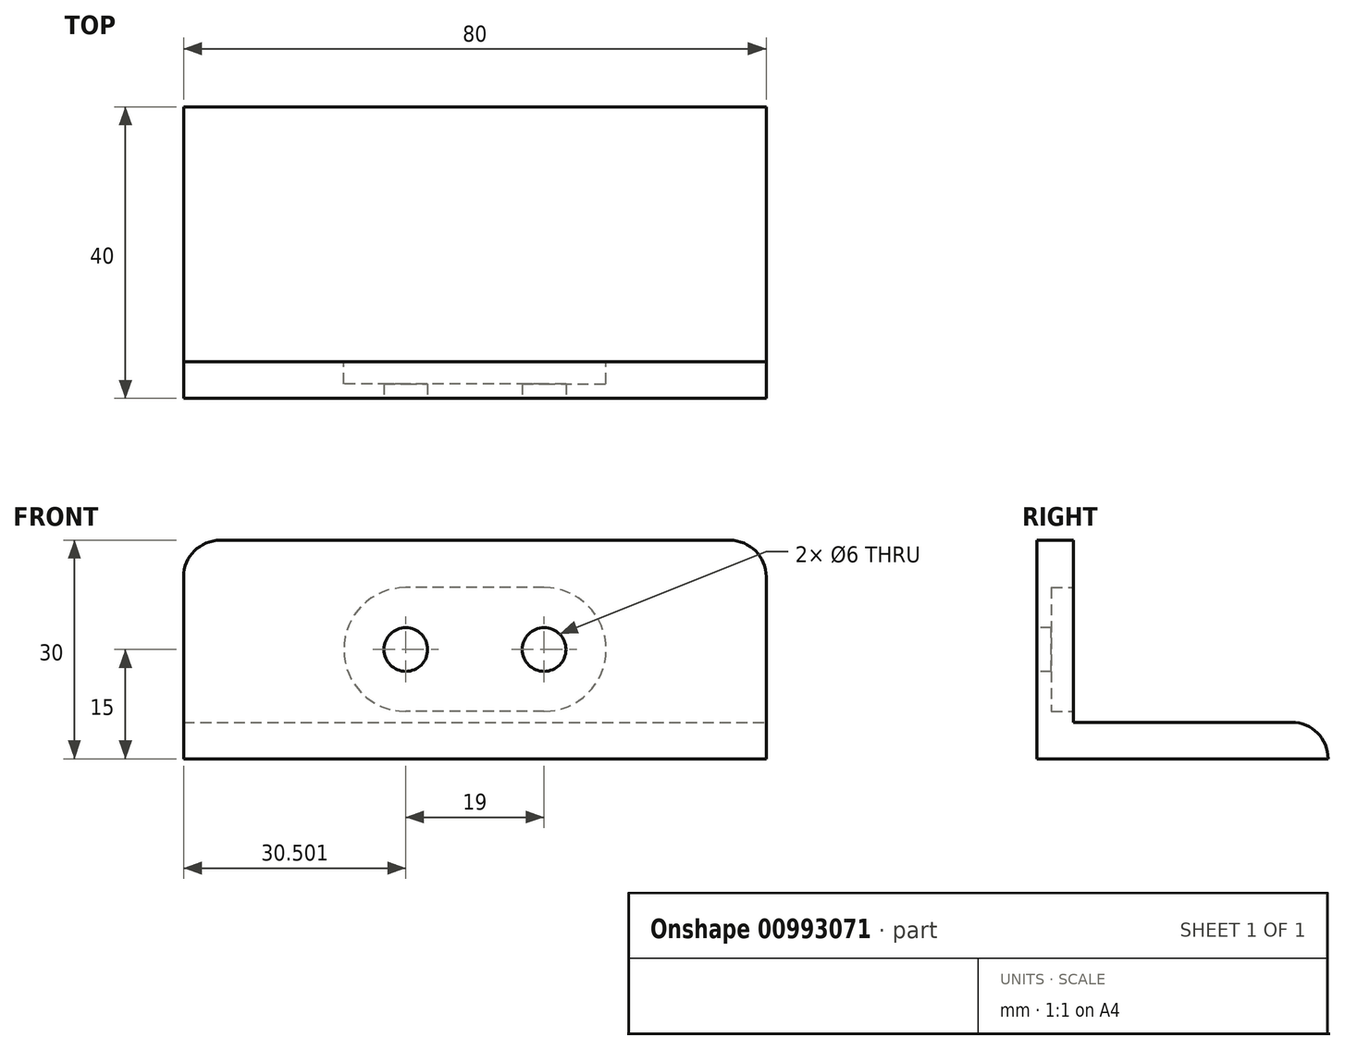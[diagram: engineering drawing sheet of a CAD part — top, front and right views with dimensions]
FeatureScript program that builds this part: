
annotation { "Feature Type Name" : "Feature", "Feature Type Description" : "" }
export const myFeature = defineFeature(function(context is Context, id is Id, definition is map)
    precondition{}
    {
        {
            var Q0;
            Q0=qCreatedBy(makeId("Top.planeOp"),FACE);
            var sketch = newSketch(context, id + "F0", { "sketchPlane" : qUnion([Q0])});
            skLineSegment(sketch, "E0.bottom", {"start": v(-41.64, 4.3) * mm, "end": v(38.36, 4.3) * mm});
            skLineSegment(sketch, "E0.top", {"start": v(-41.64, -35.7) * mm, "end": v(38.36, -35.7) * mm});
            skLineSegment(sketch, "E0.left", {"start": v(-41.64, 4.3) * mm, "end": v(-41.64, -35.7) * mm});
            skLineSegment(sketch, "E0.right", {"start": v(38.36, 4.3) * mm, "end": v(38.36, -35.7) * mm});
            skSolve(sketch);
        }
        {
            var Q0;
            Q0=makeQuery(id+"F0.imprint","IMPRINT",FACE,{"disambiguationData":[TD([[makeQuery(id+"F0.imprint","IMPRINT",EDGE,{"derivedFrom":sQuery(id+"F0.wireOp",EDGE,"E0.bottom")}),-1.0]])]});
            extrude(context, id + "F1", {"entities" : qUnion([Q0]), "oppositeDirection" : true, "depth" : 5 * mm, "offsetDistance" : 25 * mm});
        }
        {
            var Q0;
            Q0=makeQuery(id+"F1.opExtrude","SWEPT_FACE",FACE,{"disambiguationData":[OSD([sQuery(id+"F0.wireOp",EDGE,"E0.top")])]});
            var sketch = newSketch(context, id + "F2", { "sketchPlane" : qUnion([Q0])});
            skLineSegment(sketch, "E1.bottom", {"start": v(-41.64, -5) * mm, "end": v(38.36, -5) * mm});
            skLineSegment(sketch, "E1.top", {"start": v(-41.64, 25) * mm, "end": v(38.36, 25) * mm});
            skLineSegment(sketch, "E1.left", {"start": v(-41.64, -5) * mm, "end": v(-41.64, 25) * mm});
            skLineSegment(sketch, "E1.right", {"start": v(38.36, -5) * mm, "end": v(38.36, 25) * mm});
            skCircle(sketch, "E2", {"center": v(-11.14, 10) * mm, "radius": 3 * mm});
            skCircle(sketch, "E3", {"center": v(7.86, 10) * mm, "radius": 3 * mm});
            skPoint(sketch, "E4", {"position": v(-41.64, 10) * mm});
            skLineSegment(sketch, "E5", {"start": v(-11.14, 10) * mm, "end": v(-41.64, 10) * mm, "construction": true});
            skLineSegment(sketch, "E6", {"start": v(7.86, 10) * mm, "end": v(38.36, 10) * mm, "construction": true});
            skSolve(sketch);
        }
        {
            var Q0;
            {var subQ0=sQuery(id+"F2.wireOp",EDGE,"E1.top");Q0=makeQuery(id+"F2.imprint","IMPRINT",FACE,{"disambiguationData":[TD([[makeQuery(id+"F2.imprint","IMPRINT",EDGE,{"derivedFrom":subQ0}),-1.0]])]});}
            extrude(context, id + "F3", {"entities" : qUnion([Q0]), "operationType" : NewBodyOperationType.ADD, "oppositeDirection" : true, "depth" : 5 * mm, "offsetDistance" : 25 * mm});
        }
        {
            var Q0;
            Q0=makeQuery(id+"F3.opExtrude","SWEPT_EDGE",EDGE,{"disambiguationData":[OSD([sQuery(id+"F2.wireOp",EDGE,"E1.top"),sQuery(id+"F2.wireOp",EDGE,"E1.left")])]});
            var Q1;
            Q1=makeQuery(id+"F3.opExtrude","SWEPT_EDGE",EDGE,{"disambiguationData":[OSD([sQuery(id+"F2.wireOp",EDGE,"E1.top"),sQuery(id+"F2.wireOp",EDGE,"E1.right")])]});
            var Q2;
            Q2=makeQuery(id+"F1.opExtrude","CAP_EDGE",EDGE,{"disambiguationData":[OSD([sQuery(id+"F0.wireOp",EDGE,"E0.bottom")])],"isStart":true});
            fillet(context, id + "F4", {"entities" : qUnion([Q0, Q1, Q2]), "radius" : 5 * mm, "tangentPropagation" : true, "allowEdgeOverflow" : false});
        }
        {
            var Q0;
            Q0=makeQuery(id+"F3.opExtrude","CAP_FACE",FACE,{"disambiguationData":[OSD([sQuery(id+"F0.wireOp",EDGE,"E0.top"),sQuery(id+"F2.wireOp",EDGE,"E1.top"),sQuery(id+"F2.wireOp",EDGE,"E1.left"),sQuery(id+"F2.wireOp",EDGE,"E1.right"),sQuery(id+"F2.wireOp",EDGE,"E2"),sQuery(id+"F2.wireOp",EDGE,"E3")])],"isStart":false});
            var sketch = newSketch(context, id + "F5", { "sketchPlane" : qUnion([Q0])});
            skCircle(sketch, "E7", {"center": v(-7.86, 10) * mm, "radius": 8.5 * mm});
            skCircle(sketch, "E8", {"center": v(11.14, 10) * mm, "radius": 8.5 * mm});
            skLineSegment(sketch, "E9", {"start": v(-7.86, 18.5) * mm, "end": v(11.14, 18.5) * mm});
            skLineSegment(sketch, "E10", {"start": v(-7.86, 1.5) * mm, "end": v(11.14, 1.5) * mm});
            skSolve(sketch);
        }
        {
            var Q0;
            {var subQ0=sQuery(id+"F5.wireOp",EDGE,"E9");Q0=makeQuery(id+"F5.imprint","IMPRINT",FACE,{"disambiguationData":[TD([[makeQuery(id+"F5.imprint","IMPRINT",EDGE,{"derivedFrom":subQ0}),-1.0]])]});}
            var Q1;
            Q1=makeQuery(id+"F5.imprint","IMPRINT",FACE,{"disambiguationData":[TD([[makeQuery(id+"F5.imprint","IMPRINT",EDGE,{"derivedFrom":makeQuery(id+"F3.opExtrude","CAP_EDGE",EDGE,{"disambiguationData":[OSD([sQuery(id+"F2.wireOp",EDGE,"E3")])],"isStart":false})}),1.0]])]});
            var Q2;
            Q2=makeQuery(id+"F5.imprint","IMPRINT",FACE,{"disambiguationData":[TD([[makeQuery(id+"F5.imprint","IMPRINT",EDGE,{"derivedFrom":makeQuery(id+"F3.opExtrude","CAP_EDGE",EDGE,{"disambiguationData":[OSD([sQuery(id+"F2.wireOp",EDGE,"E2")])],"isStart":false})}),1.0]])]});
            extrude(context, id + "F6", {"entities" : qUnion([Q0, Q1, Q2]), "operationType" : NewBodyOperationType.REMOVE, "oppositeDirection" : true, "depth" : 3 * mm, "offsetDistance" : 25 * mm});
        }
    });
